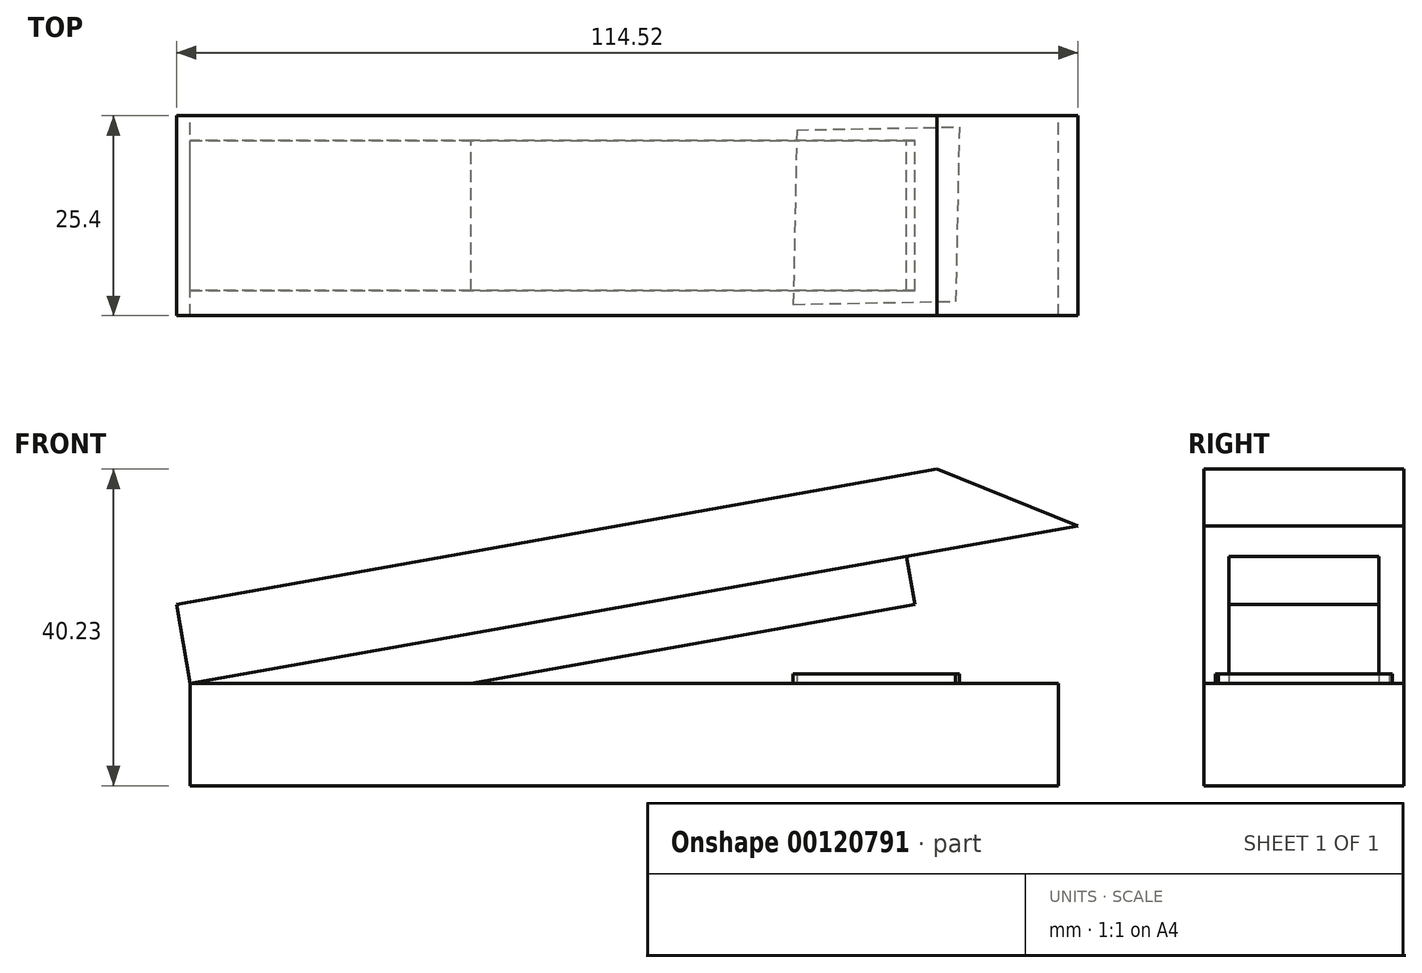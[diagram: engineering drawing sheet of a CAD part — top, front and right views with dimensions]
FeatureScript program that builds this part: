
annotation { "Feature Type Name" : "Feature", "Feature Type Description" : "" }
export const myFeature = defineFeature(function(context is Context, id is Id, definition is map)
    precondition{}
    {
        {
            var Q0;
            Q0=qCreatedBy(makeId("Front.planeOp"),FACE);
            var sketch = newSketch(context, id + "F0", { "sketchPlane" : qUnion([Q0])});
            skLineSegment(sketch, "E0.bottom", {"start": v(47.3, 8.96) * mm, "end": v(-63, 8.96) * mm});
            skLineSegment(sketch, "E0.top", {"start": v(47.3, -4.07) * mm, "end": v(-63, -4.07) * mm});
            skLineSegment(sketch, "E0.left", {"start": v(47.3, 8.96) * mm, "end": v(47.3, -4.07) * mm});
            skLineSegment(sketch, "E0.right", {"start": v(-63, 8.96) * mm, "end": v(-63, -4.07) * mm});
            skLineSegment(sketch, "E1", {"start": v(-63, 8.96) * mm, "end": v(49.76, 28.95) * mm});
            skLineSegment(sketch, "E2", {"start": v(49.76, 28.95) * mm, "end": v(31.85, 36.16) * mm});
            skLineSegment(sketch, "E3", {"start": v(31.85, 36.16) * mm, "end": v(-64.76, 18.96) * mm});
            skLineSegment(sketch, "E4", {"start": v(-64.76, 18.96) * mm, "end": v(-63, 8.96) * mm});
            skLineSegment(sketch, "E5", {"start": v(27.96, 25.09) * mm, "end": v(29.04, 18.96) * mm});
            skPoint(sketch, "E5.endSnap0", {"position": v(-6.61, 18.96) * mm});
            skLineSegment(sketch, "E6", {"start": v(29.04, 18.96) * mm, "end": v(-27.33, 8.96) * mm});
            skSolve(sketch);
        }
        {
            var Q0;
            {var subQ0=sQuery(id+"F0.wireOp",EDGE,"E2");Q0=makeQuery(id+"F0.imprint","IMPRINT",FACE,{"disambiguationData":[TD([[makeQuery(id+"F0.imprint","IMPRINT",EDGE,{"derivedFrom":subQ0}),1.0]])]});}
            var Q1;
            Q1=makeQuery(id+"F0.imprint","IMPRINT",FACE,{"disambiguationData":[TD([[makeQuery(id+"F0.imprint","IMPRINT",EDGE,{"derivedFrom":sQuery(id+"F0.wireOp",EDGE,"E0.top")}),-1.0]])]});
            extrude(context, id + "F1", {"entities" : qUnion([Q0, Q1]), "endBound" : BoundingType.SYMMETRIC, "depth" : 25.4 * mm});
        }
        {
            var Q0;
            {var subQ4=sQuery(id+"F0.wireOp",EDGE,"E5");Q0=makeQuery(id+"F0.imprint","IMPRINT",FACE,{"disambiguationData":[TD([[makeQuery(id+"F0.imprint","IMPRINT",EDGE,{"derivedFrom":subQ4}),-1.0]])]});}
            extrude(context, id + "F2", {"entities" : qUnion([Q0]), "endBound" : BoundingType.SYMMETRIC, "depth" : 19.05 * mm});
        }
        {
            var Q0;
            Q0=qCreatedBy(makeId("Top.planeOp"),FACE);
            var sketch = newSketch(context, id + "F3", { "sketchPlane" : qUnion([Q0])});
            skLineSegment(sketch, "E7.left", {"start": v(14.05, 10.88) * mm, "end": v(13.58, -11.26) * mm});
            skLineSegment(sketch, "E7.right", {"start": v(34.7, 11.26) * mm, "end": v(34.22, -10.88) * mm});
            skPoint(sketch, "E7.middle", {"position": v(24.14, 0) * mm});
            skLineSegment(sketch, "E8", {"start": v(13.58, -11.26) * mm, "end": v(24.14, 0) * mm});
            skLineSegment(sketch, "E9", {"start": v(34.7, 11.26) * mm, "end": v(24.14, 0) * mm});
            skLineSegment(sketch, "E10", {"start": v(24.14, 0) * mm, "end": v(34.22, -10.88) * mm});
            skLineSegment(sketch, "E11", {"start": v(24.14, 0) * mm, "end": v(14.05, 10.88) * mm});
            skLineSegment(sketch, "E12", {"start": v(13.58, -11.26) * mm, "end": v(34.22, -10.88) * mm});
            skLineSegment(sketch, "E13", {"start": v(14.05, 10.88) * mm, "end": v(34.7, 11.26) * mm});
            skSolve(sketch);
        }
        {
            var Q0;
            Q0 = qSketchRegion(id + "F3", true);
            extrude(context, id + "F4", {"entities" : qUnion([Q0]), "operationType" : NewBodyOperationType.ADD, "depth" : 10.16 * mm});
        }
    });
